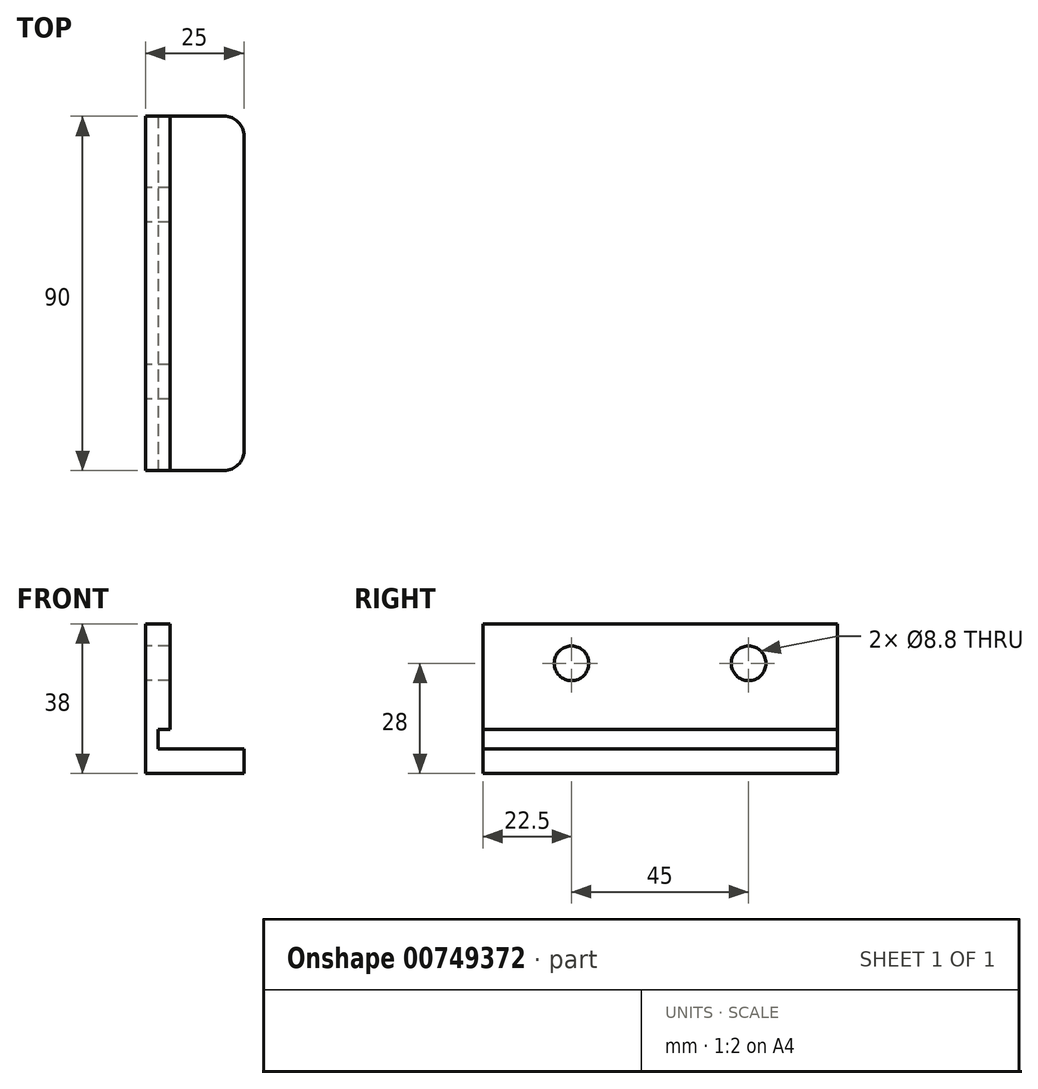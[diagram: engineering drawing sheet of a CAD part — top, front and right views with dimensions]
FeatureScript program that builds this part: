
annotation { "Feature Type Name" : "Feature", "Feature Type Description" : "" }
export const myFeature = defineFeature(function(context is Context, id is Id, definition is map)
    precondition{}
    {
        {
            var Q0;
            Q0=qCreatedBy(makeId("Front.planeOp"),FACE);
            var sketch = newSketch(context, id + "F0", { "sketchPlane" : qUnion([Q0])});
            skLineSegment(sketch, "E0", {"start": v(0, 0) * mm, "end": v(0, 38) * mm});
            skLineSegment(sketch, "E1", {"start": v(0, 38) * mm, "end": v(6.2, 38) * mm});
            skLineSegment(sketch, "E2", {"start": v(0, 0) * mm, "end": v(25, 0) * mm});
            skLineSegment(sketch, "E3", {"start": v(25, 0) * mm, "end": v(25, 6.2) * mm});
            skLineSegment(sketch, "E4", {"start": v(6.2, 38) * mm, "end": v(6.2, 6.2) * mm});
            skLineSegment(sketch, "E5", {"start": v(25, 6.2) * mm, "end": v(6.2, 6.2) * mm});
            skSolve(sketch);
        }
        {
            var Q0;
            Q0 = qSketchRegion(id + "F0", true);
            extrude(context, id + "F1", {"entities" : qUnion([Q0]), "depth" : 90 * mm, "offsetDistance" : 25 * mm});
        }
        {
            var Q0;
            Q0=makeQuery(id+"F1.opExtrude","SWEPT_FACE",FACE,{"disambiguationData":[OSD([sQuery(id+"F0.wireOp",EDGE,"E0")])]});
            var sketch = newSketch(context, id + "F2", { "sketchPlane" : qUnion([Q0])});
            skPoint(sketch, "E6", {"position": v(67.5, 28) * mm});
            skPoint(sketch, "E7", {"position": v(22.5, 28) * mm});
            skSolve(sketch);
        }
        {
            var Q0;
            Q0=sQuery(id+"F2.wireOp",VERTEX,"E6");
            var Q1;
            Q1=sQuery(id+"F2.wireOp",VERTEX,"E7");
            var Q2;
            Q2=makeQuery(id+"F1.opExtrude","SWEPT_BODY",BODY,{"disambiguationData":[OSD([sQuery(id+"F0.wireOp",EDGE,"E0"),sQuery(id+"F0.wireOp",EDGE,"E1"),sQuery(id+"F0.wireOp",EDGE,"E2"),sQuery(id+"F0.wireOp",EDGE,"E3"),sQuery(id+"F0.wireOp",EDGE,"E4"),sQuery(id+"F0.wireOp",EDGE,"E5")])]});
            hole(context, id + "F3", {"style" : HoleStyle.SIMPLE, "endStyle" : HoleEndStyle.THROUGH, "standardTappedOrClearance" : lookupTablePath({ "standard" : "ISO", "fit" : "Normal", "size" : "M8", "type" : "Clearance" }), "standardBlindInLast" : lookupTablePath({ "fit" : "Standard", "standard" : "ISO", "size" : "M8", "type" : "Clearance" }), "holeDiameter" : 8.8 * mm, "majorDiameter" : 5 * mm, "isTappedThrough" : true, "tappedDepth" : 13.25 * mm, "tapClearance" : 3, "locations" : qUnion([Q0, Q1]), "scope" : qUnion([Q2])});
        }
        {
            var Q0;
            Q0=makeQuery(id+"F1.opExtrude","CAP_EDGE",EDGE,{"disambiguationData":[OSD([sQuery(id+"F0.wireOp",EDGE,"E3")])],"isStart":false});
            var Q1;
            Q1=makeQuery(id+"F1.opExtrude","CAP_EDGE",EDGE,{"disambiguationData":[OSD([sQuery(id+"F0.wireOp",EDGE,"E3")])],"isStart":true});
            fillet(context, id + "F4", {"entities" : qUnion([Q0, Q1]), "radius" : 5 * mm, "tangentPropagation" : true, "allowEdgeOverflow" : false});
        }
        {
            var Q0;
            Q0=makeQuery(id+"F1.opExtrude","CAP_FACE",FACE,{"disambiguationData":[OSD([sQuery(id+"F0.wireOp",EDGE,"E0"),sQuery(id+"F0.wireOp",EDGE,"E1"),sQuery(id+"F0.wireOp",EDGE,"E2"),sQuery(id+"F0.wireOp",EDGE,"E3"),sQuery(id+"F0.wireOp",EDGE,"E4"),sQuery(id+"F0.wireOp",EDGE,"E5")])],"isStart":false});
            var sketch = newSketch(context, id + "F5", { "sketchPlane" : qUnion([Q0])});
            skLineSegment(sketch, "E8", {"start": v(6.2, 6.2) * mm, "end": v(3.2, 6.2) * mm});
            skLineSegment(sketch, "E9", {"start": v(3.2, 6.2) * mm, "end": v(3.2, 11.2) * mm});
            skLineSegment(sketch, "E10", {"start": v(6.2, 11.2) * mm, "end": v(3.2, 11.2) * mm});
            skLineSegment(sketch, "E11", {"start": v(6.2, 11.2) * mm, "end": v(6.2, 6.2) * mm});
            skSolve(sketch);
        }
        {
            var Q0;
            Q0=makeQuery(id+"F5.imprint","IMPRINT",FACE,{"disambiguationData":[TD([[makeQuery(id+"F5.imprint","IMPRINT",EDGE,{"derivedFrom":sQuery(id+"F5.wireOp",EDGE,"E8")}),-1.0]])]});
            extrude(context, id + "F6", {"entities" : qUnion([Q0]), "operationType" : NewBodyOperationType.REMOVE, "oppositeDirection" : true, "depth" : 90 * mm, "offsetDistance" : 25 * mm});
        }
    });
